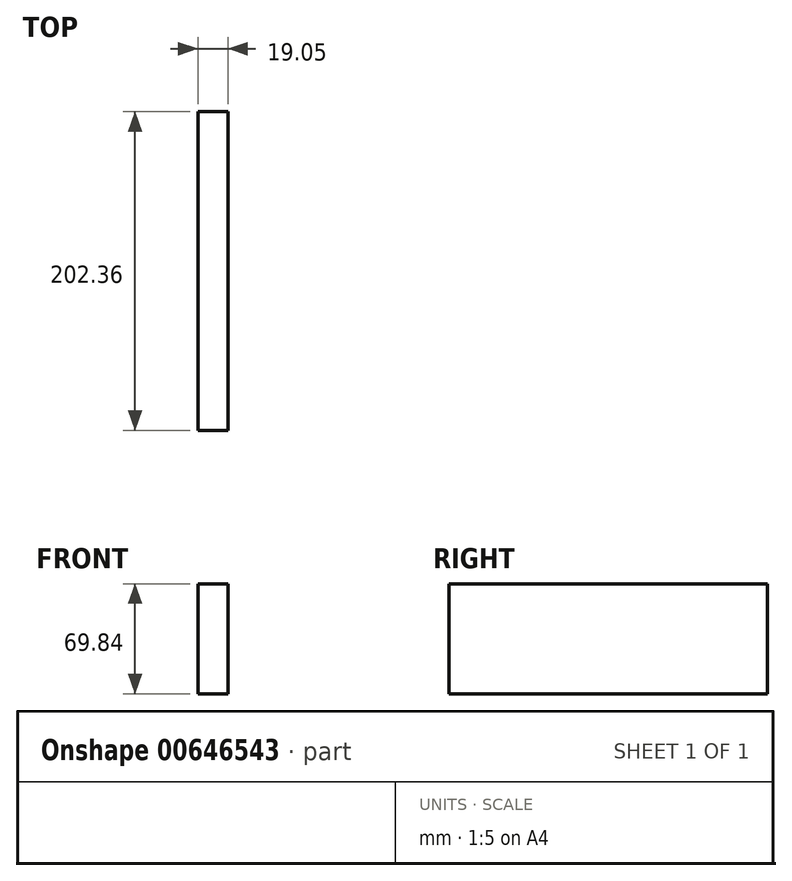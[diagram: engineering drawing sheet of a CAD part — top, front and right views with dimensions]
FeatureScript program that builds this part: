
annotation { "Feature Type Name" : "Feature", "Feature Type Description" : "" }
export const myFeature = defineFeature(function(context is Context, id is Id, definition is map)
    precondition{}
    {
        {
            var Q0;
            Q0=qCreatedBy(makeId("Right.planeOp"),FACE);
            var sketch = newSketch(context, id + "F0", { "sketchPlane" : qUnion([Q0])});
            skLineSegment(sketch, "E0.bottom", {"start": v(101.18, 34.93) * mm, "end": v(-101.18, 34.93) * mm});
            skLineSegment(sketch, "E0.top", {"start": v(101.18, -34.93) * mm, "end": v(-101.18, -34.93) * mm});
            skLineSegment(sketch, "E0.left", {"start": v(101.18, 34.92) * mm, "end": v(101.18, -34.92) * mm});
            skLineSegment(sketch, "E0.right", {"start": v(-101.18, 34.92) * mm, "end": v(-101.18, -34.92) * mm});
            skPoint(sketch, "E0.middle", {"position": v(0, 0) * mm});
            skSolve(sketch);
        }
        {
            var Q0;
            Q0=makeQuery(id+"F0.imprint","IMPRINT",FACE,{"disambiguationData":[TD([[makeQuery(id+"F0.imprint","IMPRINT",EDGE,{"derivedFrom":sQuery(id+"F0.wireOp",EDGE,"E0.bottom")}),1.0]])]});
            extrude(context, id + "F1", {"entities" : qUnion([Q0]), "depth" : 19.05 * mm, "offsetDistance" : 25.4 * mm});
        }
    });
